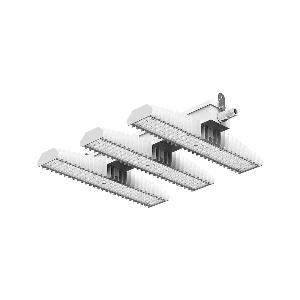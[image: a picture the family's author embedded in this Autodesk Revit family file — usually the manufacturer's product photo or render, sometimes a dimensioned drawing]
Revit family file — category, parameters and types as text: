
# Revit family: 3f_filippi_-_3f_lem_medio_3f_filippi_-_58894_-_3f_lem_3_led_150_cr_medio
name_source: partatom
category: Lighting Fixtures
units: mm (PartAtom-declared; Revit-internal decimal feet)

## family parameters
Cut with Voids When Loaded = No
Host = Face
Light Source = No
Part Type = Normal
Room Calculation Point = No
Round Connector Dimension = Use Diameter
Shared = No

## types (1)
- 3F Filippi - 3F LEM Medio (1 x LED, 24944 lm, 165 W, 4000 K)
    Apparent Load = 165 VA
    Approval mark = CE
    CIE Flux Codes = 83 96 99 100 100
    Color Rendering = 80
    Color Temperature = 4000 K
    Control Gear = Electronic ballast
    Default Elevation = 1800 mm
    Description = Industrial luminaire with high light output and high luminous efficiency designed with the most innovative technologies for environments with temperature up to 55°C.

ILLUMINOTECHNICAL
Luminous efficiency 100% (DLOR 100%, ULOR 0%).
Initial luminous flux of the luminaire 24944 lm.
Medium distribution with rectangular shape.
Installation Interdistance Transv.D = 1.02 x hu - Long.D = 1.06 x hu.
Tabular UGR (CIE 117 - 4H-8H; S=0.25H; 70/50/20): RUG 19.2 - 18.8.
Beam angle: 65° - 67°.
Luminous efficacy 151 lm/W.
Lifetime (L93/B10): 30000 h. (tq+25°C)
Lifetime (L90/B10): 50000 h. (tq+25°C)
Lifetime (L85/B10): 80000 h. (tq+25°C)
Lifetime (L80/B10): 100000 h. (tq+25°C)
Lifetime (L85/B10): 50000 h. (tq+55°C)
Sudden decreased luminous flux after 50000 hours: 0% (C0).
Photobiological safety in compliance with IEC/TR 62778: RG0 risk exempt, (IEC 62471).
In compliance with IEC/EN 62722-2-1 - IEC/EN 62717 standards.

SOURCE
3 Mid-Power linear LED modules 50W/840.
Energy efficiency class (UE 2019/2020 - UE 2019/2015): C.
CIE 13.3 Colour rendering index: CRI >80 (R9 <50%).
IES TM-30 Fidelity Index: Rf = 84 Rg = 95.
CCT nominal colour temperature 4000 K.
Colour initial tolerance (MacAdam): SDCM 3.

MECHANICAL
Passive modular heatsinks in die-casted aluminium, painted in white colour.
To optimize the thermal management of the LED module, the heatsinks are oversized and provided with self-cleaning of cooling fins.
Wiring body in aluminium and galvanised steel anchored solidly to the sinks and thermally separated.
3F Lens lenses with high luminous efficiency, transparent methacrylate (PMMA), fixed to the LED modules.
Fixing brackets in stainless steel.
Luminaire with limited surface temperature. - D - (EN 60598-2-24)
Dimensions: 657x542 mm, height 129 mm. Weight 13.375 kg.
IP65 protection degree.
Mechanical strength to impacts IK06 (1 joule).
Glow-wire test resistance 650°C.

ELECTRICAL
Halogen Free electronic wiring 230V-50/60Hz, power factor 0.97, THD <25%, constant output current, class I, 2 driver.
Power of the luminaire 165 W.
ENEC - CE.
SAFE FLICKER: PstLM=<1 and SVM=<0.4 (IEC TR 61547-1 and IEC TR 63158), to ensure a more comfortable and safe light.
Luminaire compliant with EN 60598-2-22 for power supply from a centralised emergency system CPSS (Central Power Supply System), not incorporated in the luminaire - high risk areas excluded. The default power and flux are 100% in AC and 100% in DC.
Ambient temperature from -30°C to +55°C.
Temperature class T6 max 85°C.
Quick connection via M20 3P connector with 9-13 mm tightening range.
Power unit positioned on a separate compartment by the LED module to ensure optimum temperatures of cabling components, to be inspectable and maintainable.
Relative humidity UR: <85%.

INSTALLATION
Ceiling / Suspended / Wall.
All accessories dedicated to this product are available on the Catalog and on our website www.3F-Filippi.com.

APPLICATIONS
In commercial environments, exhibition and industrial areas, stores, open areas.
Applications with high ambient temperature up to 55°C.
Environments in which it is necessary a total protection against falling fragments (eg environments with foodstuffs or machines with moving parts or with extreme temperature changes), use luminaires with polycarbonate lenses.

WARNING
Fixture not suitable for cold stores with an ambient temperature <0°C and/or relative humidity >85%.
Luminaire designed for disposal/recycling at end-of-life.
Replaceable (LED only) light source by a professional. Replaceable control gear by a professional.
    Height = 129 mm
    Lamp = 1 x LED
    Lamp Light Flux = 24944 lm
    Lamp Power = 165 W
    Lamp count = 1
    Length = 657 mm
    Lifetime = 50000 h
    Luminous efficacy = 151 lm/W
    Manufacturer = 3F Filippi
    ModVariant = No
    Model = 3F Filippi - 58894 - 3F LEM 3 LED 150 CR MEDIO
    Mounting Place = Ceiling
    Mounting Type = Pendant
    Number of Poles = 1
    OnlyDefault = Yes
    Power Factor = 1
    Product Name = 3F Filippi - 3F LEM Medio
    Product group = pendant luminaire
    ProductGroupID = 9
    Protection Class = Protection class I
    Protection Degree = IP 65
    RLX_Detail_Level = 1
    RLX_Emergency_Light_Flux = 0 lm
    RLX_Emergency_Type = 0
    RLX_Emergency_Type_DB = No
    RlxData = <blob elided: 100805 chars, md5=13d2c41e>
    Socket = socket
    Standby Power = 0 W
    System Light Flux = 24944 lm
    System Power = 165 W
    Type Comments = Product without accessories
    Type Image = 3f_filippi_-_lem_3.jpg
    URL = http://relux.com
    VarID = ---
    Voltage = 0 V
    Weight = 0.00 kg
    Width = 542 mm

## geometry (parser evidence)
native form markers: Blend x4, Sweep x11
no freeform markers — native parametric forms only
